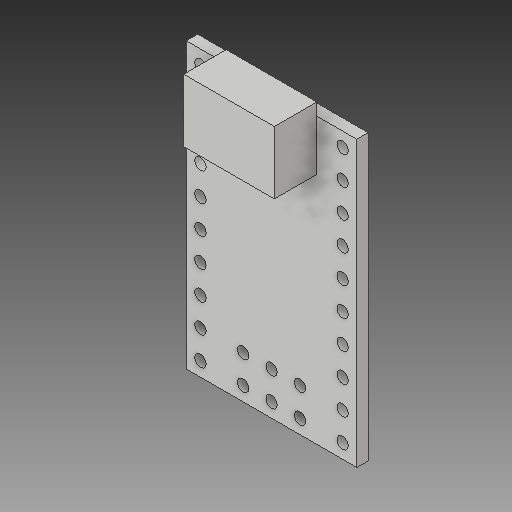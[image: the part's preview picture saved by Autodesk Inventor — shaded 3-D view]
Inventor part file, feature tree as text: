
AUTODESK INVENTOR PART (.ipt)
format: ipt  version: 2018.1 (Build 221171000, 171)  size: 165,888 bytes
history: native  units: mm
features: extrude x3, sketch x3, other x1
ambient origin geometry x8: Origin, YZ Plane, XZ Plane, XY Plane, X Axis, Y Axis, Z Axis, Center Point
bodies: Body1 (feature_tree)
feature tree (7):
  other  "ソリッド1"
  extrude  "押し出し1"  Depth=15.24mm
  extrude  "押し出し2"  Depth=25.4mm
  extrude  "押し出し3"  Depth=1.02mm TaperAngle=0.0deg
  sketch  "スケッチ1"
  sketch  "スケッチ2"
  sketch  "スケッチ3"
